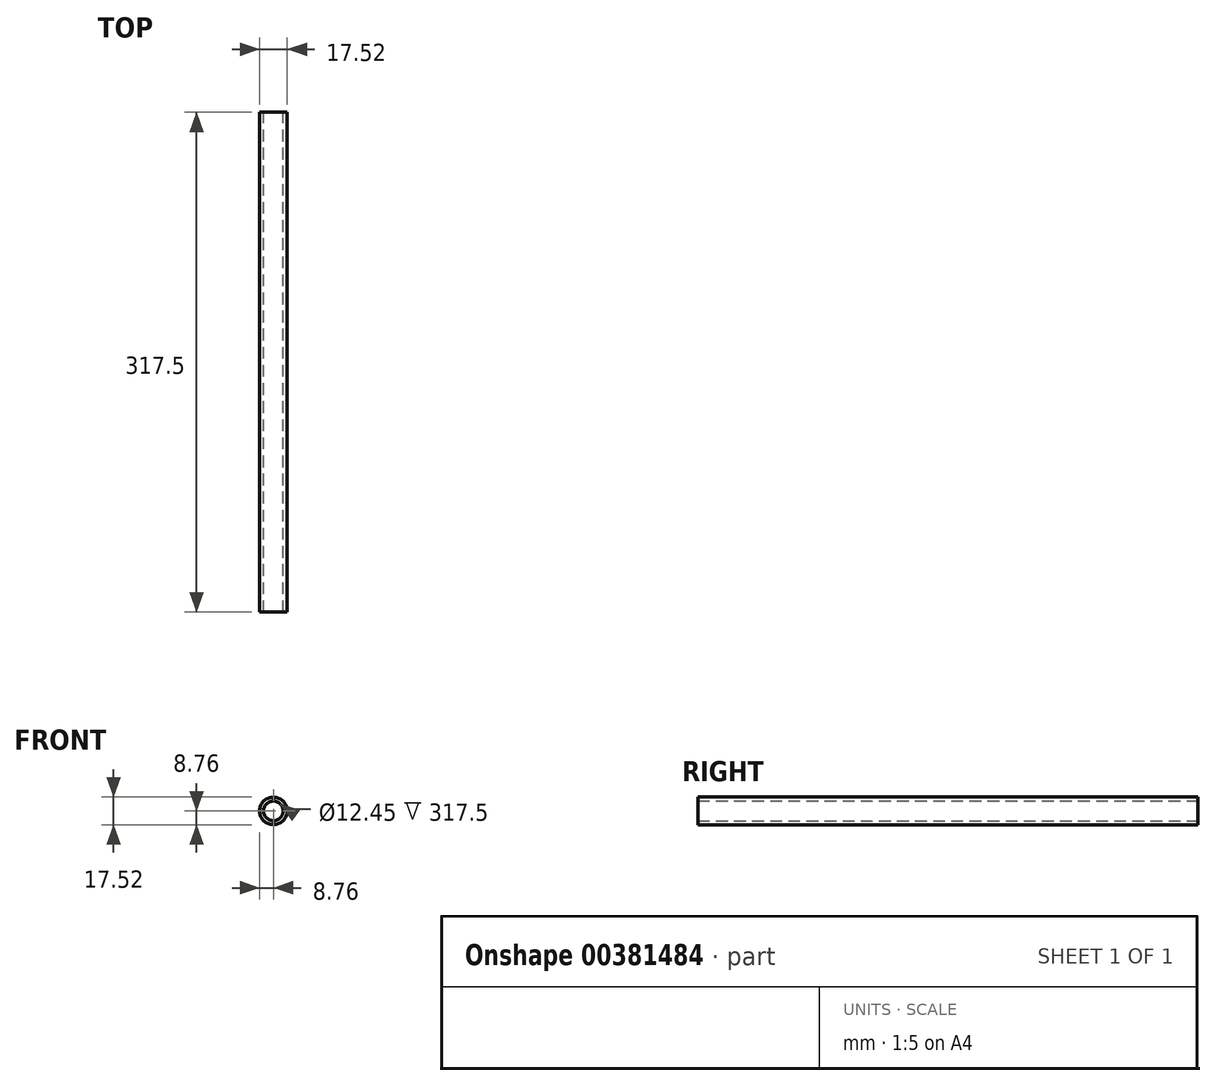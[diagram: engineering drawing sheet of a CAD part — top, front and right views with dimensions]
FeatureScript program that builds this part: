
annotation { "Feature Type Name" : "Feature", "Feature Type Description" : "" }
export const myFeature = defineFeature(function(context is Context, id is Id, definition is map)
    precondition{}
    {
        {
            var Q0;
            Q0=qCreatedBy(makeId("Front.planeOp"),FACE);
            var sketch = newSketch(context, id + "F0", { "sketchPlane" : qUnion([Q0])});
            skCircle(sketch, "E0", {"center": v(0, 0) * mm, "radius": 8.76 * mm});
            skCircle(sketch, "E1", {"center": v(0, 0) * mm, "radius": 6.22 * mm});
            skSolve(sketch);
        }
        {
            var Q0;
            Q0 = qSketchRegion(id + "F0", true);
            extrude(context, id + "F1", {"entities" : qUnion([Q0]), "depth" : 317.5 * mm});
        }
    });
